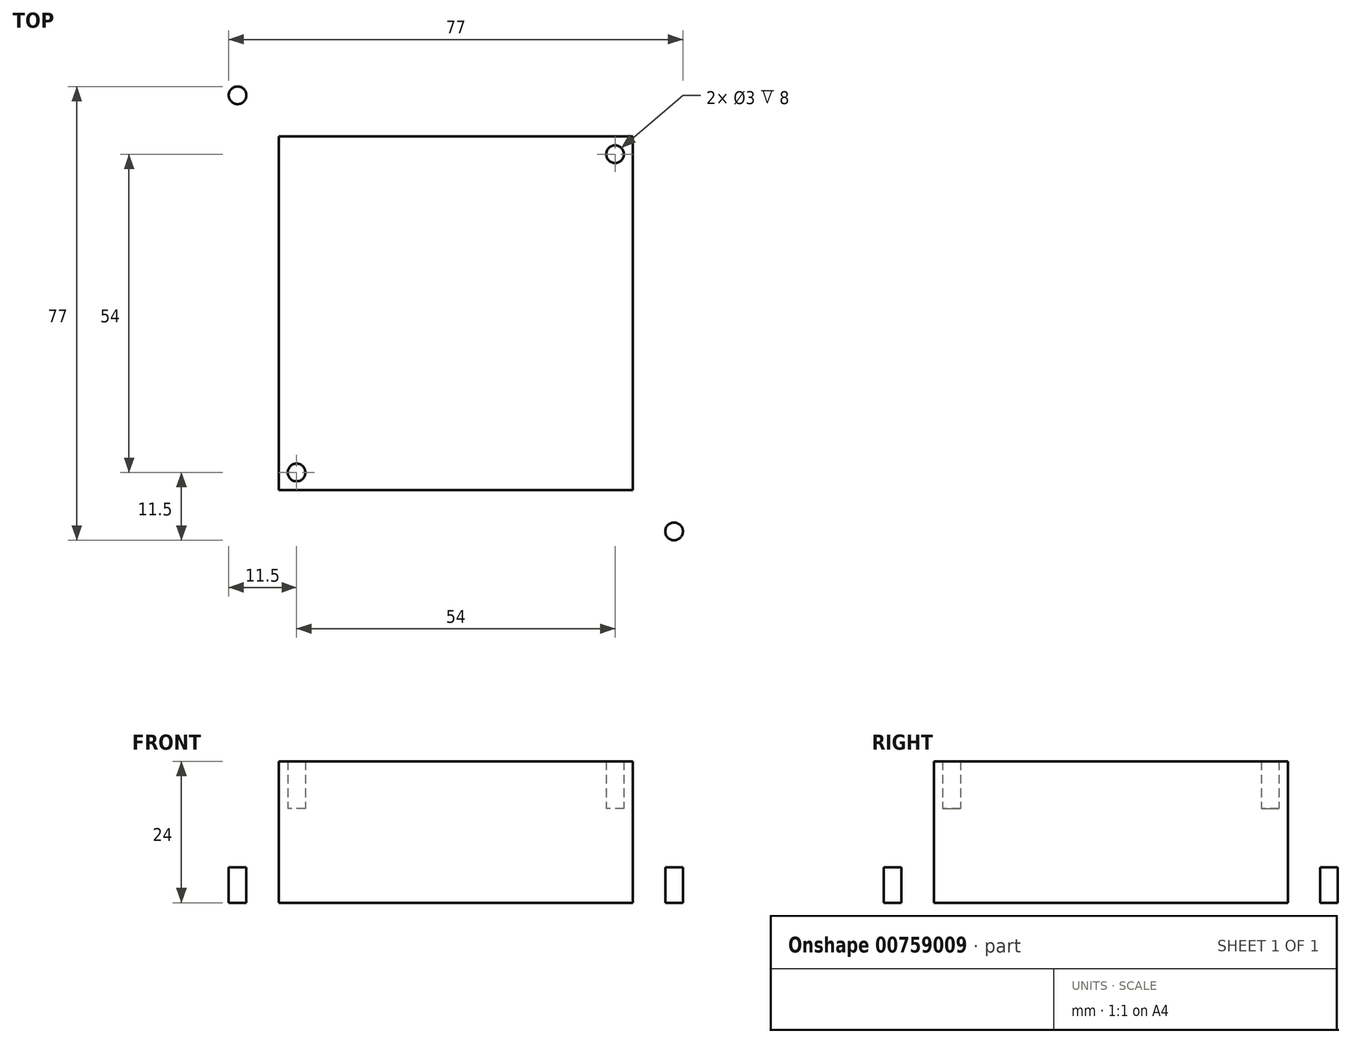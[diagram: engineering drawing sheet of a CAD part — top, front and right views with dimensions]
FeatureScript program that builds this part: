
annotation { "Feature Type Name" : "Feature", "Feature Type Description" : "" }
export const myFeature = defineFeature(function(context is Context, id is Id, definition is map)
    precondition{}
    {
        {
            var Q0;
            Q0=qCreatedBy(makeId("Top.planeOp"),FACE);
            var sketch = newSketch(context, id + "F0", { "sketchPlane" : qUnion([Q0])});
            skLineSegment(sketch, "E0.bottom", {"start": v(-40, 40) * mm, "end": v(40, 40) * mm});
            skLineSegment(sketch, "E0.top", {"start": v(-40, -40) * mm, "end": v(40, -40) * mm});
            skLineSegment(sketch, "E0.left", {"start": v(-40, 40) * mm, "end": v(-40, -40) * mm});
            skLineSegment(sketch, "E0.right", {"start": v(40, 40) * mm, "end": v(40, -40) * mm});
            skPoint(sketch, "E0.middle", {"position": v(0, 0) * mm});
            skSolve(sketch);
        }
        {
            var Q0;
            Q0=makeQuery(id+"F0.imprint","IMPRINT",FACE,{"disambiguationData":[TD([[makeQuery(id+"F0.imprint","IMPRINT",EDGE,{"derivedFrom":sQuery(id+"F0.wireOp",EDGE,"E0.bottom")}),-1.0]])]});
            extrude(context, id + "F1", {"entities" : qUnion([Q0]), "depth" : 6 * mm, "offsetDistance" : 25 * mm});
        }
        {
            var Q0;
            Q0=makeQuery(id+"F1.opExtrude","CAP_FACE",FACE,{"disambiguationData":[OSD([sQuery(id+"F0.wireOp",EDGE,"E0.bottom"),sQuery(id+"F0.wireOp",EDGE,"E0.top"),sQuery(id+"F0.wireOp",EDGE,"E0.left"),sQuery(id+"F0.wireOp",EDGE,"E0.right")])],"isStart":false});
            var sketch = newSketch(context, id + "F2", { "sketchPlane" : qUnion([Q0])});
            skLineSegment(sketch, "E1.bottom", {"start": v(-30, 30) * mm, "end": v(30, 30) * mm});
            skLineSegment(sketch, "E1.top", {"start": v(-30, -30) * mm, "end": v(30, -30) * mm});
            skLineSegment(sketch, "E1.left", {"start": v(-30, 30) * mm, "end": v(-30, -30) * mm});
            skLineSegment(sketch, "E1.right", {"start": v(30, 30) * mm, "end": v(30, -30) * mm});
            skPoint(sketch, "E1.middle", {"position": v(0, 0) * mm});
            skSolve(sketch);
        }
        {
            var Q0;
            Q0=makeQuery(id+"F2.imprint","IMPRINT",FACE,{"disambiguationData":[TD([[makeQuery(id+"F2.imprint","IMPRINT",EDGE,{"derivedFrom":sQuery(id+"F2.wireOp",EDGE,"E1.bottom")}),-1.0]])]});
            extrude(context, id + "F3", {"entities" : qUnion([Q0]), "operationType" : NewBodyOperationType.ADD, "depth" : 10 * mm, "offsetDistance" : 25 * mm});
        }
        {
            var Q0;
            Q0=makeQuery(id+"F3.opExtrude","CAP_FACE",FACE,{"disambiguationData":[OSD([sQuery(id+"F2.wireOp",EDGE,"E1.bottom"),sQuery(id+"F2.wireOp",EDGE,"E1.top"),sQuery(id+"F2.wireOp",EDGE,"E1.left"),sQuery(id+"F2.wireOp",EDGE,"E1.right")])],"isStart":false});
            var sketch = newSketch(context, id + "F4", { "sketchPlane" : qUnion([Q0])});
            skCircle(sketch, "E2", {"center": v(27, -27) * mm, "radius": 1.5 * mm});
            skCircle(sketch, "E3.MirrorC", {"center": v(-27, -27) * mm, "radius": 1.5 * mm});
            skCircle(sketch, "E4.MirrorC", {"center": v(-27, 27) * mm, "radius": 1.5 * mm});
            skCircle(sketch, "E5.MirrorC", {"center": v(27, 27) * mm, "radius": 1.5 * mm});
            skSolve(sketch);
        }
        {
            var Q0;
            Q0=makeQuery(id+"F4.imprint","IMPRINT",FACE,{"disambiguationData":[TD([[makeQuery(id+"F4.imprint","IMPRINT",EDGE,{"derivedFrom":sQuery(id+"F4.wireOp",EDGE,"E3.MirrorC")}),-1.0]])]});
            var Q1;
            Q1=makeQuery(id+"F4.imprint","IMPRINT",FACE,{"disambiguationData":[TD([[makeQuery(id+"F4.imprint","IMPRINT",EDGE,{"derivedFrom":sQuery(id+"F4.wireOp",EDGE,"E2")}),1.0]])]});
            var Q2;
            Q2=makeQuery(id+"F4.imprint","IMPRINT",FACE,{"disambiguationData":[TD([[makeQuery(id+"F4.imprint","IMPRINT",EDGE,{"derivedFrom":sQuery(id+"F4.wireOp",EDGE,"E5.MirrorC")}),-1.0]])]});
            var Q3;
            Q3=makeQuery(id+"F4.imprint","IMPRINT",FACE,{"disambiguationData":[TD([[makeQuery(id+"F4.imprint","IMPRINT",EDGE,{"derivedFrom":sQuery(id+"F4.wireOp",EDGE,"E4.MirrorC")}),1.0]])]});
            extrude(context, id + "F5", {"entities" : qUnion([Q0, Q1, Q2, Q3]), "operationType" : NewBodyOperationType.ADD, "depth" : 8 * mm, "offsetDistance" : 25 * mm});
        }
        {
            var Q0;
            Q0=makeQuery(id+"F1.opExtrude","CAP_FACE",FACE,{"disambiguationData":[OSD([sQuery(id+"F0.wireOp",EDGE,"E0.bottom"),sQuery(id+"F0.wireOp",EDGE,"E0.top"),sQuery(id+"F0.wireOp",EDGE,"E0.left"),sQuery(id+"F0.wireOp",EDGE,"E0.right")])],"isStart":false});
            var sketch = newSketch(context, id + "F6", { "sketchPlane" : qUnion([Q0])});
            skCircle(sketch, "E6", {"center": v(37, 37) * mm, "radius": 1.5 * mm});
            skCircle(sketch, "E7.MirrorC", {"center": v(37, -37) * mm, "radius": 1.5 * mm});
            skCircle(sketch, "E8.MirrorC", {"center": v(-37, 37) * mm, "radius": 1.5 * mm});
            skCircle(sketch, "E9.MirrorC", {"center": v(-37, -37) * mm, "radius": 1.5 * mm});
            skSolve(sketch);
        }
        {
            var Q0;
            Q0=makeQuery(id+"F6.imprint","IMPRINT",FACE,{"disambiguationData":[TD([[makeQuery(id+"F6.imprint","IMPRINT",EDGE,{"derivedFrom":sQuery(id+"F6.wireOp",EDGE,"E8.MirrorC")}),-1.0]])]});
            var Q1;
            Q1=makeQuery(id+"F6.imprint","IMPRINT",FACE,{"disambiguationData":[TD([[makeQuery(id+"F6.imprint","IMPRINT",EDGE,{"derivedFrom":sQuery(id+"F6.wireOp",EDGE,"E6")}),1.0]])]});
            var Q2;
            Q2=makeQuery(id+"F6.imprint","IMPRINT",FACE,{"disambiguationData":[TD([[makeQuery(id+"F6.imprint","IMPRINT",EDGE,{"derivedFrom":sQuery(id+"F6.wireOp",EDGE,"E9.MirrorC")}),1.0]])]});
            var Q3;
            Q3=makeQuery(id+"F6.imprint","IMPRINT",FACE,{"disambiguationData":[TD([[makeQuery(id+"F6.imprint","IMPRINT",EDGE,{"derivedFrom":sQuery(id+"F6.wireOp",EDGE,"E7.MirrorC")}),-1.0]])]});
            extrude(context, id + "F7", {"entities" : qUnion([Q0, Q1, Q2, Q3]), "operationType" : NewBodyOperationType.REMOVE, "oppositeDirection" : true, "depth" : 6 * mm, "offsetDistance" : 25 * mm});
        }
    });
